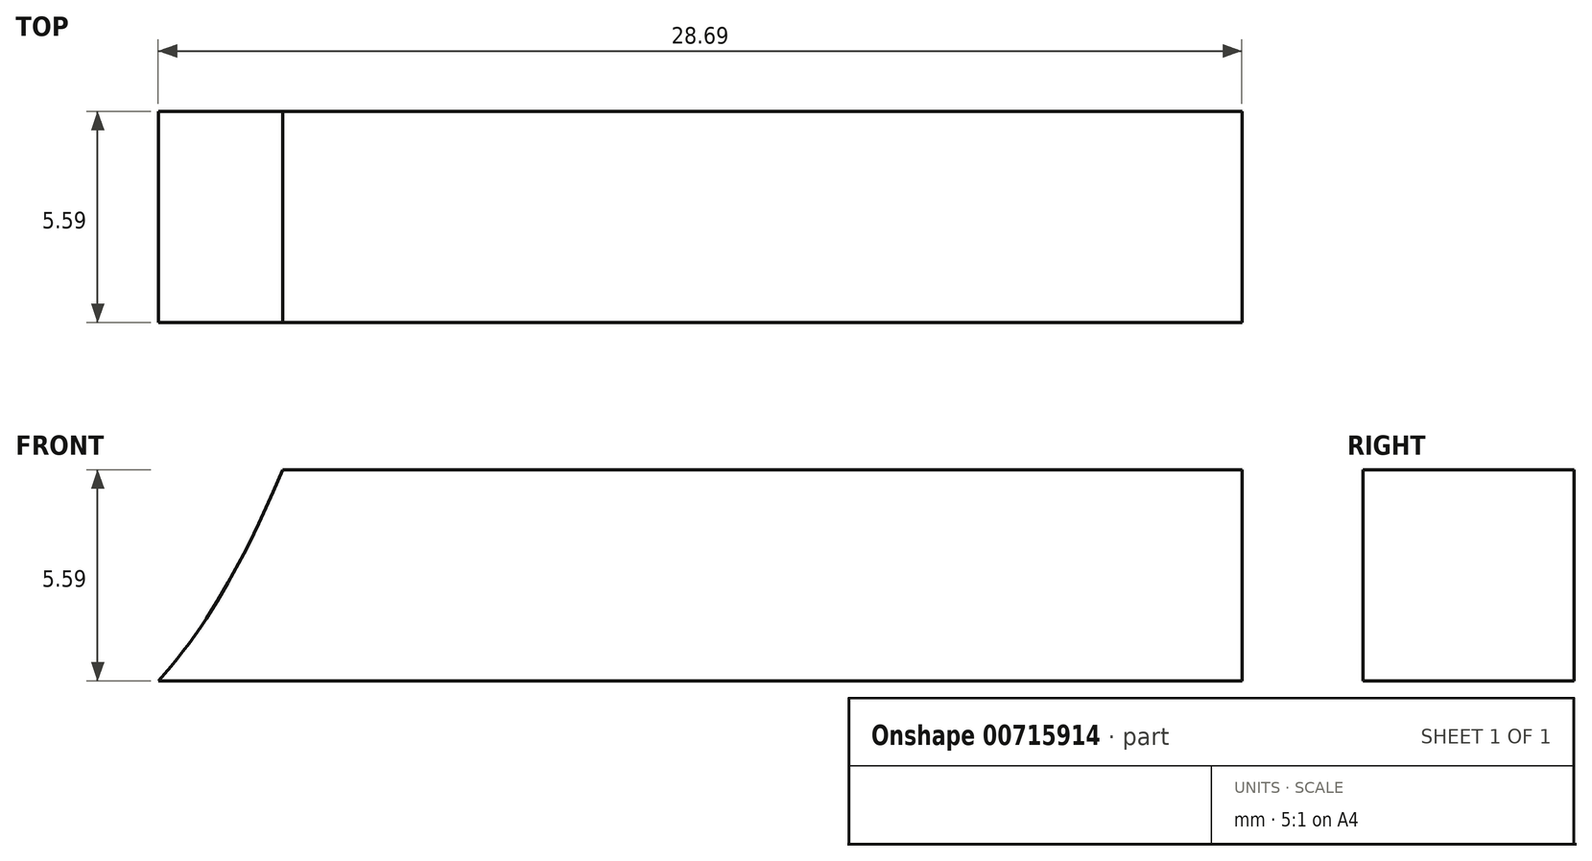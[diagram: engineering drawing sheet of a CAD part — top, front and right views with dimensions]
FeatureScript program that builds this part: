
annotation { "Feature Type Name" : "Feature", "Feature Type Description" : "" }
export const myFeature = defineFeature(function(context is Context, id is Id, definition is map)
    precondition{}
    {
        {
            var Q0;
            Q0=qCreatedBy(makeId("Front.planeOp"),FACE);
            var sketch = newSketch(context, id + "F0", { "sketchPlane" : qUnion([Q0])});
            skFitSpline(sketch, "E0", {"points": [v(23.14, 153.41) * mm, v(41.93, 165.53) * mm, v(65.56, 170.99) * mm, v(86.76, 180.08) * mm, v(111, 189.16) * mm, v(131, 189.77) * mm, v(146.75, 184.92) * mm, v(164.32, 178.26) * mm, v(178.86, 172.2) * mm, v(200.68, 169.77) * mm, v(218.25, 168.56) * mm, v(234, 167.96) * mm, v(250.36, 167.35) * mm, v(267.94, 167.35) * mm, v(284.3, 166.74) * mm, v(299.44, 166.74) * mm, v(314.6, 167.35) * mm, v(329.74, 171.6) * mm, v(342.47, 204.92) * mm, v(356.4, 212.8) * mm, v(364.28, 193.4) * mm, v(368.52, 177.05) * mm, v(372.16, 164.93) * mm, v(364.88, 152.8) * mm, v(226.13, 134.63) * mm, v(118.88, 134.02) * mm, v(48.6, 140.69) * mm, v(23.14, 153.41) * mm]});
            skLineSegment(sketch, "E1", {"start": v(88.9, 166.88) * mm, "end": v(190.5, 166.88) * mm});
            skLineSegment(sketch, "E2", {"start": v(88.9, 166.88) * mm, "end": v(88.9, 161.3) * mm});
            skLineSegment(sketch, "E3", {"start": v(88.9, 161.3) * mm, "end": v(190.5, 161.3) * mm});
            skLineSegment(sketch, "E4", {"start": v(190.5, 166.88) * mm, "end": v(190.5, 161.3) * mm});
            skLineSegment(sketch, "E5", {"start": v(332.87, 177) * mm, "end": v(358.27, 177) * mm});
            skLineSegment(sketch, "E6", {"start": v(358.27, 177) * mm, "end": v(358.27, 171.41) * mm});
            skLineSegment(sketch, "E7", {"start": v(358.27, 171.41) * mm, "end": v(329.58, 171.41) * mm});
            skSolve(sketch);
        }
        {
            var Q0;
            Q0=makeQuery(id+"F0.imprint","IMPRINT",FACE,{"disambiguationData":[TD([[makeQuery(id+"F0.imprint","IMPRINT",EDGE,{"derivedFrom":sQuery(id+"F0.wireOp",EDGE,"E0")}),-1.0]])]});
            extrude(context, id + "F1", {"entities" : qUnion([Q0]), "depth" : 5.6 * mm, "offsetDistance" : 25.4 * mm});
        }
    });
